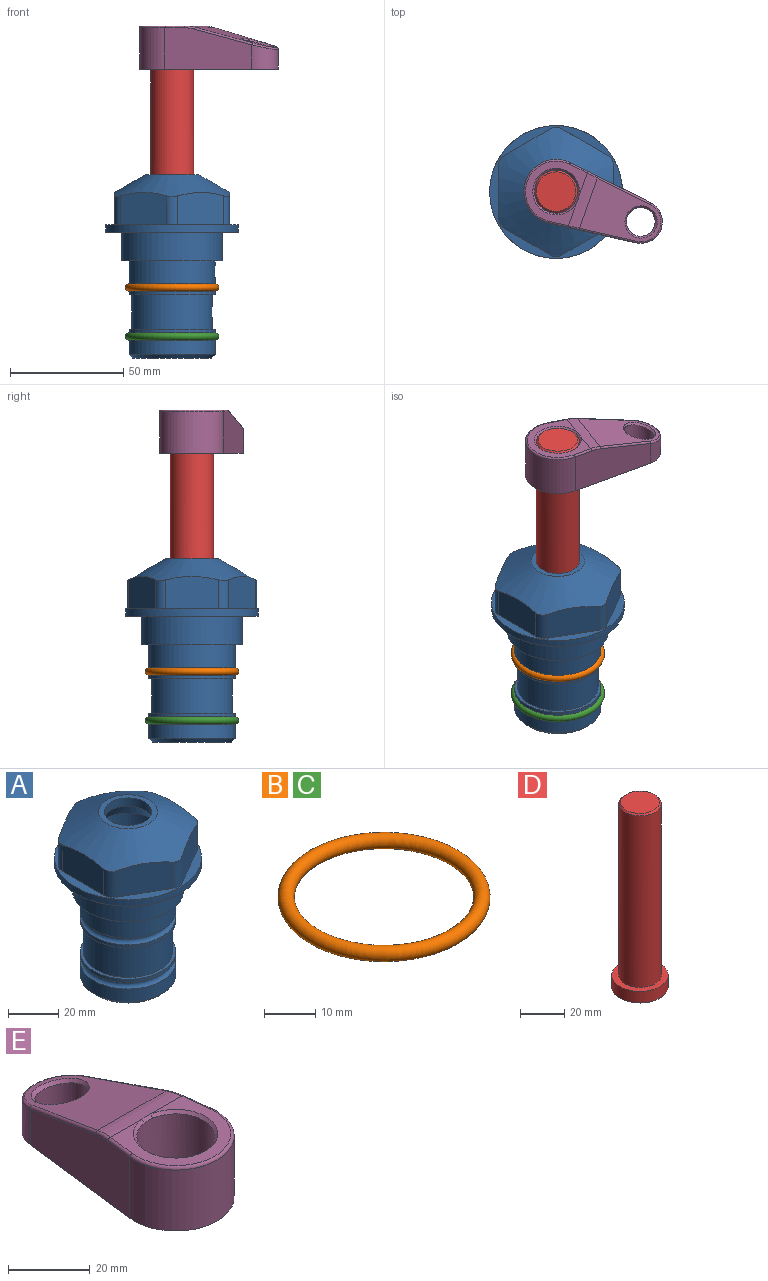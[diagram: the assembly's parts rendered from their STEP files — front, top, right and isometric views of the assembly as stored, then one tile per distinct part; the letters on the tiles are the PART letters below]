
ASSEMBLY  parts=5 mates=4
PART A: 36 faces, bbox 58.7x58.7x81 mm
  f0: cylinder r=17.78mm len=35.56mm, axis (0,0,1), area 1670.8mm2, adj f23,f24,f31
  f1: cylinder r=19.05mm len=38.1mm, axis (0,0,1), area 1191.9mm2, adj f26,f27,f30
  f2: plane 58.66x58.66mm, normal (0,0,-1), area 1150.6mm2, adj f3,f28
  f3: cylinder r=29.33mm len=58.66mm, axis (0,0,-1), area 585.1mm2, adj f2,f4
  f4: plane 58.66x58.66mm, normal (0,0,1), area 475.9mm2, adj f3,f5,f6,f7,f8,f9,f10,f11
  f5: plane 20.32x14.34mm, normal (-0.5,0.87,0), area 324.4mm2, adj f4,f15,f16,f17
  f6: plane 20.32x14.34mm, normal (0.5,0.87,0), area 324.4mm2, adj f4,f14,f15,f17
  f7: plane 23.48x14.34mm, normal (1,0,0), area 324.4mm2, adj f4,f13,f14,f17
  f8: plane 20.32x14.34mm, normal (0.5,-0.87,0), area 324.4mm2, adj f4,f12,f13,f17
  f9: plane 20.32x14.34mm, normal (-0.5,-0.87,0), area 324.4mm2, adj f4,f11,f12,f17
  f10: plane 23.48x14.34mm, normal (-1,0,0), area 324.4mm2, adj f4,f11,f16,f17
  f11: cylinder r=5.08mm len=12.85mm, axis (0,0,-1), area 67.2mm2, adj f4,f9,f10,f17
  f12: cylinder r=5.08mm len=12.85mm, axis (0,0,-1), area 67.2mm2, adj f4,f8,f9,f17
  f13: cylinder r=5.08mm len=12.85mm, axis (0,0,-1), area 67.2mm2, adj f4,f7,f8,f17
  f14: cylinder r=5.08mm len=12.85mm, axis (0,0,-1), area 67.2mm2, adj f4,f6,f7,f17
  f15: cylinder r=5.08mm len=12.85mm, axis (0,0,-1), area 67.2mm2, adj f4,f5,f6,f17
  f16: cylinder r=5.08mm len=12.85mm, axis (0,0,-1), area 67.2mm2, adj f4,f5,f10,f17
  f17: cone r=11.73mm half-angle=60deg, axis (0,0,-1), area 2071.8mm2, adj f5,f6,f7,f8,f9,f10,f11,f12
  f18: plane 23.46x23.46mm, normal (0,0,1), area 147.4mm2, adj f17,f35
  f19: plane 34.93x34.93mm, normal (0,0,-1), area 958mm2, adj f29
  f20: cylinder r=19.05mm len=38.1mm, axis (0,0,1), area 760.1mm2, adj f21,f29
  f21: torus R=19.05mm, axis (0,0,1), area 565.3mm2, adj f20,f22
  f22: cylinder r=19.05mm len=38.1mm, axis (0,0,1), area 190mm2, adj f21,f23
  f23: plane 38.1x38.1mm, normal (0,0,1), area 146.9mm2, adj f0,f22
  f24: plane 38.1x38.1mm, normal (0,0,-1), area 146.9mm2, adj f0,f25
  f25: cylinder r=19.05mm len=38.1mm, axis (0,0,1), area 190mm2, adj f24,f26
  f26: torus R=19.05mm, axis (0,0,1), area 565.3mm2, adj f1,f25
  f27: plane 44.45x44.45mm, normal (0,0,-1), area 411.7mm2, adj f1,f28
  f28: cylinder r=22.23mm len=44.45mm, axis (0,0,1), area 1773.5mm2, adj f2,f27
  f29: cone r=19.05mm half-angle=45deg, axis (0,0,1), area 257.5mm2, adj f19,f20
  f30: cylinder r=3.17mm len=6.75mm, axis (-1,0,0), area 128mm2, adj f1,f33
  f31: cylinder r=3.17mm len=6.35mm, axis (-1,0,0), area 102.5mm2, adj f0,f33
  f32: plane 25.4x25.4mm, normal (0,0,1), area 506.7mm2, adj f33
  f33: cylinder r=12.7mm len=66.42mm, axis (0,0,-1), area 5236.2mm2, adj f30,f31,f32,f34
  f34: cone r=9.53mm half-angle=30deg, axis (0,0,-1), area 443.4mm2, adj f33,f35
  f35: cylinder r=9.53mm len=19.05mm, axis (0,0,-1), area 240.9mm2, adj f18,f34
PART B: 1 faces, bbox 44.7x44.7x3.2 mm
  f0: torus R=19.05mm, axis (0,0,1), area 1193.9mm2
PART C: same geometry as B
PART D: 6 faces, bbox 25.4x25.4x101.6 mm
  f0: plane 17.46x17.46mm, normal (0,0,1), area 239.5mm2, adj f5
  f1: plane 25.4x25.4mm, normal (0,0,-1), area 506.7mm2, adj f2
  f2: cylinder r=12.7mm len=25.4mm, axis (0,0,1), area 506.7mm2, adj f1,f3
  f3: plane 25.4x25.4mm, normal (0,0,1), area 221.7mm2, adj f2,f4
  f4: cylinder r=9.53mm len=94.46mm, axis (0,0,1), area 5653mm2, adj f3,f5
  f5: cone r=8.73mm half-angle=45deg, axis (0,0,-1), area 64.4mm2, adj f0,f4
PART E: 31 faces, bbox 31.7x65.5x19.8 mm
  f0: plane 39.12x18.26mm, normal (0.99,0.12,0), area 612.2mm2, adj f1,f4,f7,f11,f13,f15
  f1: cylinder r=9.53mm len=18.91mm, axis (0,0,-1), area 296.1mm2, adj f0,f2,f7,f17
  f2: plane 39.12x18.26mm, normal (-0.99,0.12,0), area 612.2mm2, adj f1,f4,f7,f12,f14,f16
  f3: cylinder r=6.35mm len=12.7mm, axis (0,0,-1), area 362.4mm2, adj f7,f18
  f4: cylinder r=14.29mm len=28.58mm, axis (0,0,-1), area 882.2mm2, adj f0,f2,f7,f10
  f5: cylinder r=9.53mm len=19.05mm, axis (0,0,-1), area 1092.6mm2, adj f7,f19,f20
  f6: plane 26.99x23.69mm, normal (0,0,1), area 216.2mm2, adj f9,f10,f11,f12,f19
  f7: plane 63.5x28.58mm, normal (0,0,-1), area 661.8mm2, adj f0,f1,f2,f3,f4,f5,f22,f23
  f8: plane 33.52x23.6mm, normal (0,0.26,0.97), area 486mm2, adj f9,f15,f16,f17,f18
  f9: cylinder r=19.05mm len=24.72mm, axis (1,0,0), area 120.4mm2, adj f6,f8,f13,f14,f20
  f10: torus R=13.49mm, axis (0,0,1), area 59mm2, adj f4,f6,f11,f12
  f11: cylinder r=0.79mm len=8.67mm, axis (0.12,-0.99,0), area 10.8mm2, adj f0,f6,f10,f13
  f12: cylinder r=0.79mm len=8.67mm, axis (0.12,0.99,0), area 10.8mm2, adj f2,f6,f10,f14
  f13: bspline ~4.95x1.42mm, area 6.1mm2, adj f0,f9,f11,f15
  f14: bspline ~4.95x1.42mm, area 6.1mm2, adj f2,f9,f12,f16
  f15: cylinder r=0.79mm len=25.95mm, axis (0.12,-0.96,0.26), area 32.9mm2, adj f0,f8,f13,f17
  f16: cylinder r=0.79mm len=25.95mm, axis (0.12,0.96,-0.26), area 32.9mm2, adj f2,f8,f14,f17
  f17: bspline ~18.91x8.38mm, area 30mm2, adj f1,f8,f15,f16
  f18: bspline ~14.29x14.29mm, area 48.3mm2, adj f3,f8
  f19: cone r=9.53mm half-angle=45deg, axis (0,0,1), area 66.5mm2, adj f5,f6,f20
  f20: bspline ~3.22x0.96mm, area 3.5mm2, adj f5,f9,f19
  f21: plane 2.75x2.72mm, normal (0,0,-1), area 2.9mm2, adj f23,f25,f28
  f22: plane 23.05x15.88mm, normal (-0.99,-0.12,0), area 323.6mm2, adj f7,f25,f26,f27,f28,f29
  f23: plane 23.05x15.88mm, normal (0.99,-0.12,0), area 323.6mm2, adj f7,f21,f25,f27,f28,f30
  f24: cylinder r=9.53mm len=10.69mm, axis (0,0,-1), area 114.7mm2, adj f7,f27,f29,f30
  f25: cylinder r=12.7mm len=20.59mm, axis (0,0,-1), area 381.1mm2, adj f7,f21,f22,f23,f26,f28
  f26: plane 2.75x2.72mm, normal (0,0,-1), area 2.9mm2, adj f22,f25,f28
  f27: plane 19.72x18.37mm, normal (0,-0.26,-0.97), area 291.8mm2, adj f22,f23,f24,f28,f29,f30
  f28: cylinder r=15.88mm len=19.92mm, axis (1,0,0), area 54.8mm2, adj f21,f22,f23,f25,f26,f27
  f29: cylinder r=1.59mm len=11mm, axis (0,0,-1), area 34.7mm2, adj f7,f22,f24,f27
  f30: cylinder r=1.59mm len=11mm, axis (0,0,-1), area 34.7mm2, adj f7,f23,f24,f27
PLACE A at identity fixed
PLACE B at identity
PLACE C t=(0,0,-21.59)mm
PLACE D rot(axis=(0,0,-1),109.6deg) t=(0,0,27.55)mm
PLACE E rot(axis=(0,0,-1),109.6deg) t=(0,0,27.55)mm
MATE cylindrical A.f0 <-> D.f2  axis (0,0,1) through (0,0,-50.55)mm
MATE fastened C.f0 <-> A.f0  axis (0,0,1) through (0,0,-46.1)mm
MATE fastened D.f2 <-> E.f4  axis (0,0,-1) through (0,0,90.26)mm
MATE fastened B.f0 <-> A.f0  axis (0,0,1) through (0,0,-24.51)mm
